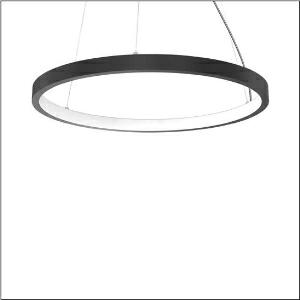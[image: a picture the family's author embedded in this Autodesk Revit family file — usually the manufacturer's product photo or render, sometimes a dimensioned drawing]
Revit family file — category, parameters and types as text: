
# Revit family: silica_r__21_ring-i_5pjbi4d3104a_5ad9
name_source: partatom
category: Lighting Fixtures
units: mm (PartAtom-declared; Revit-internal decimal feet)

## family parameters
Cut with Voids When Loaded = No
Host = Face
Light Source = No
Part Type = Normal
Room Calculation Point = No
Round Connector Dimension = Use Diameter
Shared = No

## types (1)
- Silica® 21 Ring-I (1 x LED, 8890 lm, 140 W, 4000K)
    Apparent Load = 140 VA
    CIE Flux Codes = 22 48 76 50 101
    Color Rendering = 80
    Color Temperature = 4000K
    Default Elevation = 1800 mm
    Description = Silica® 21 Ring-I, suspended luminaire, of PMMA, frosted, light emission: inner ring side luminous distribution, primary light characteristic: symmetric, installation type: suspended mounting, LED, rated luminous flux: 8.890lm, luminous efficacy: 64lm/W, light colour: 840, colour temperature: 4000K, with terminal, 5-pole, mains connection: 230V, AC/DC, 0/50..60Hz, rated input power: 140W, housing, of extruded aluminium section, jet black (RAL 9005), diameter: 1.470mm, ceiling canopy, jet black (RAL 9005), protection rating (lamp compartment): IP40, insulation class (complete): insulation class I (protective earthing), certification: CE, impact resistance: IK02, permissible operating ambient temperature: 0..+35°C, packaging unit: 1 piece
    Height = 48 mm  [stored 0.15748 ft]
    Lamp = 1 x LED
    Lamp Light Flux = 8890 lm
    Lamp Power = 140 W
    Lamp count = 1
    Length = 1470 mm
    Luminous efficacy = 64 lm/W
    Manufacturer = Siteco
    ModVariant = No
    Model = 5PJBI4D3104A
    Mounting Place = Ceiling
    Mounting Type = Pendant
    Number of Poles = 1
    OnlyDefault = Yes
    Power Factor = 1
    Product Name = Silica® 21 Ring-I
    Product group = suspended luminaire
    ProductGroupID = 904
    Protection Class = Protection class I
    Protection Degree = IP 40
    RLX_Detail_Level = 1
    RLX_Emergency_Light_Flux = 0 lm
    RLX_Emergency_Type = 0
    RLX_Emergency_Type_DB = No
    RlxData = <blob elided: 20373 chars, md5=359c87b1>
    Socket = socket
    Standby Power = 0 W
    System Light Flux = 8890 lm
    System Power = 140 W
    Type Comments = Product without accessories
    Type Image = l_1258373.jpg
    URL = http://relux.com
    VarID = ---
    Voltage = 0 V
    Weight = 0.00 kg
    Width = 0 mm  [stored 0 ft]

note: [stored X ft] marks values corroborated as IEEE doubles in the binary element streams (Revit-internal decimal feet)

## geometry (parser evidence)
native form markers: Blend x4, Sweep x14
no freeform markers — native parametric forms only
